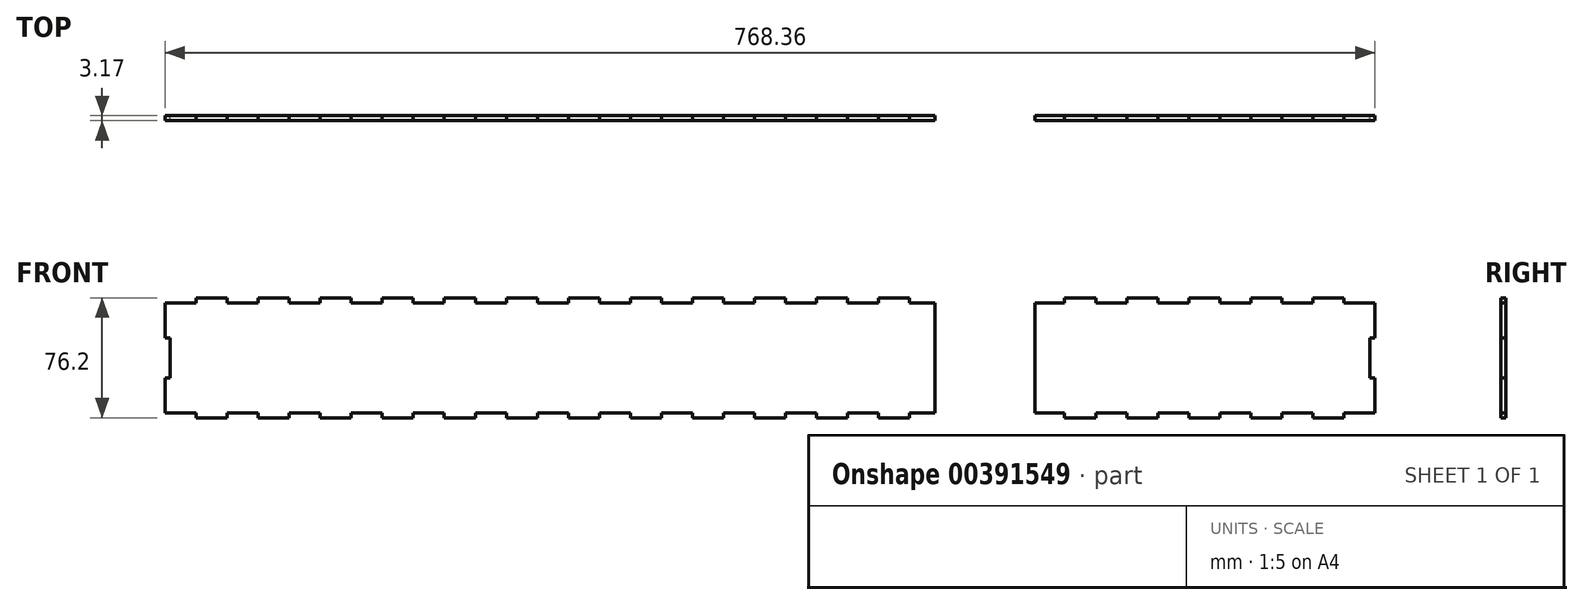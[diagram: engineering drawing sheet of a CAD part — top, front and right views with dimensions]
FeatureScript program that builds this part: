
annotation { "Feature Type Name" : "Feature", "Feature Type Description" : "" }
export const myFeature = defineFeature(function(context is Context, id is Id, definition is map)
    precondition{}
    {
        {
            var Q0;
            Q0=qCreatedBy(makeId("Front.planeOp"),FACE);
            var sketch = newSketch(context, id + "F0", { "sketchPlane" : qUnion([Q0])});
            skPoint(sketch, "E0.middle", {"position": v(0, 0) * mm});
            skLineSegment(sketch, "E1", {"start": v(-384.18, 12.7) * mm, "end": v(-381, 12.7) * mm});
            skLineSegment(sketch, "E2", {"start": v(-381, 12.7) * mm, "end": v(-381, -12.7) * mm});
            skLineSegment(sketch, "E3", {"start": v(-381, -12.7) * mm, "end": v(-384.18, -12.7) * mm});
            skLineSegment(sketch, "E4", {"start": v(-384.18, 34.92) * mm, "end": v(-364.47, 34.92) * mm});
            skLineSegment(sketch, "E5", {"start": v(-364.47, 34.92) * mm, "end": v(-364.47, 38.1) * mm});
            skLineSegment(sketch, "E6", {"start": v(-364.47, 38.1) * mm, "end": v(-344.77, 38.1) * mm});
            skLineSegment(sketch, "E7", {"start": v(-344.77, 38.1) * mm, "end": v(-344.77, 34.93) * mm});
            skLineSegment(sketch, "E8", {"start": v(-384.18, 38.1) * mm, "end": v(384.17, 38.1) * mm, "construction": true});
            skLineSegment(sketch, "E9.1.0.0", {"start": v(-344.77, 34.92) * mm, "end": v(-325.07, 34.92) * mm});
            skLineSegment(sketch, "E9.1.0.1", {"start": v(-325.07, 34.92) * mm, "end": v(-325.07, 38.1) * mm});
            skLineSegment(sketch, "E9.1.0.2", {"start": v(-325.07, 38.1) * mm, "end": v(-305.37, 38.1) * mm});
            skLineSegment(sketch, "E9.1.0.3", {"start": v(-305.37, 38.1) * mm, "end": v(-305.37, 34.93) * mm});
            skLineSegment(sketch, "E9.2.0.0", {"start": v(-305.37, 34.92) * mm, "end": v(-285.67, 34.92) * mm});
            skLineSegment(sketch, "E9.2.0.1", {"start": v(-285.67, 34.92) * mm, "end": v(-285.67, 38.1) * mm});
            skLineSegment(sketch, "E9.2.0.2", {"start": v(-285.67, 38.1) * mm, "end": v(-265.97, 38.1) * mm});
            skLineSegment(sketch, "E9.2.0.3", {"start": v(-265.97, 38.1) * mm, "end": v(-265.97, 34.93) * mm});
            skLineSegment(sketch, "E9.3.0.0", {"start": v(-265.97, 34.92) * mm, "end": v(-246.27, 34.92) * mm});
            skLineSegment(sketch, "E9.3.0.1", {"start": v(-246.27, 34.92) * mm, "end": v(-246.27, 38.1) * mm});
            skLineSegment(sketch, "E9.3.0.2", {"start": v(-246.27, 38.1) * mm, "end": v(-226.56, 38.1) * mm});
            skLineSegment(sketch, "E9.3.0.3", {"start": v(-226.56, 38.1) * mm, "end": v(-226.56, 34.93) * mm});
            skLineSegment(sketch, "E9.4.0.0", {"start": v(-226.56, 34.92) * mm, "end": v(-206.86, 34.92) * mm});
            skLineSegment(sketch, "E9.4.0.1", {"start": v(-206.86, 34.92) * mm, "end": v(-206.86, 38.1) * mm});
            skLineSegment(sketch, "E9.4.0.2", {"start": v(-206.86, 38.1) * mm, "end": v(-187.16, 38.1) * mm});
            skLineSegment(sketch, "E9.4.0.3", {"start": v(-187.16, 38.1) * mm, "end": v(-187.16, 34.93) * mm});
            skLineSegment(sketch, "E9.5.0.0", {"start": v(-187.16, 34.92) * mm, "end": v(-167.46, 34.92) * mm});
            skLineSegment(sketch, "E9.5.0.1", {"start": v(-167.46, 34.92) * mm, "end": v(-167.46, 38.1) * mm});
            skLineSegment(sketch, "E9.5.0.2", {"start": v(-167.46, 38.1) * mm, "end": v(-147.76, 38.1) * mm});
            skLineSegment(sketch, "E9.5.0.3", {"start": v(-147.76, 38.1) * mm, "end": v(-147.76, 34.93) * mm});
            skLineSegment(sketch, "E9.6.0.0", {"start": v(-147.76, 34.92) * mm, "end": v(-128.06, 34.92) * mm});
            skLineSegment(sketch, "E9.6.0.1", {"start": v(-128.06, 34.92) * mm, "end": v(-128.06, 38.1) * mm});
            skLineSegment(sketch, "E9.6.0.2", {"start": v(-128.06, 38.1) * mm, "end": v(-108.36, 38.1) * mm});
            skLineSegment(sketch, "E9.6.0.3", {"start": v(-108.36, 38.1) * mm, "end": v(-108.36, 34.93) * mm});
            skLineSegment(sketch, "E9.7.0.0", {"start": v(-108.36, 34.92) * mm, "end": v(-88.66, 34.92) * mm});
            skLineSegment(sketch, "E9.7.0.1", {"start": v(-88.66, 34.92) * mm, "end": v(-88.66, 38.1) * mm});
            skLineSegment(sketch, "E9.7.0.2", {"start": v(-88.66, 38.1) * mm, "end": v(-68.95, 38.1) * mm});
            skLineSegment(sketch, "E9.7.0.3", {"start": v(-68.95, 38.1) * mm, "end": v(-68.95, 34.93) * mm});
            skLineSegment(sketch, "E9.8.0.0", {"start": v(-68.95, 34.92) * mm, "end": v(-49.25, 34.92) * mm});
            skLineSegment(sketch, "E9.8.0.1", {"start": v(-49.25, 34.92) * mm, "end": v(-49.25, 38.1) * mm});
            skLineSegment(sketch, "E9.8.0.2", {"start": v(-49.25, 38.1) * mm, "end": v(-29.55, 38.1) * mm});
            skLineSegment(sketch, "E9.8.0.3", {"start": v(-29.55, 38.1) * mm, "end": v(-29.55, 34.93) * mm});
            skLineSegment(sketch, "E9.9.0.0", {"start": v(-29.55, 34.92) * mm, "end": v(-9.85, 34.92) * mm});
            skLineSegment(sketch, "E9.9.0.1", {"start": v(-9.85, 34.92) * mm, "end": v(-9.85, 38.1) * mm});
            skLineSegment(sketch, "E9.9.0.2", {"start": v(-9.85, 38.1) * mm, "end": v(9.85, 38.1) * mm});
            skLineSegment(sketch, "E9.9.0.3", {"start": v(9.85, 38.1) * mm, "end": v(9.85, 34.93) * mm});
            skLineSegment(sketch, "E9.10.0.0", {"start": v(9.85, 34.92) * mm, "end": v(29.55, 34.92) * mm});
            skLineSegment(sketch, "E9.10.0.1", {"start": v(29.55, 34.92) * mm, "end": v(29.55, 38.1) * mm});
            skLineSegment(sketch, "E9.10.0.2", {"start": v(29.55, 38.1) * mm, "end": v(49.25, 38.1) * mm});
            skLineSegment(sketch, "E9.10.0.3", {"start": v(49.25, 38.1) * mm, "end": v(49.25, 34.93) * mm});
            skLineSegment(sketch, "E9.11.0.0", {"start": v(49.25, 34.92) * mm, "end": v(68.95, 34.92) * mm});
            skLineSegment(sketch, "E9.11.0.1", {"start": v(68.95, 34.92) * mm, "end": v(68.95, 38.1) * mm});
            skLineSegment(sketch, "E9.11.0.2", {"start": v(68.95, 38.1) * mm, "end": v(88.66, 38.1) * mm});
            skLineSegment(sketch, "E9.11.0.3", {"start": v(88.66, 38.1) * mm, "end": v(88.66, 34.93) * mm});
            skLineSegment(sketch, "E9.12.0.0", {"start": v(88.66, 34.92) * mm, "end": v(108.36, 34.92) * mm});
            skLineSegment(sketch, "E9.12.0.1", {"start": v(108.36, 34.92) * mm, "end": v(108.36, 38.1) * mm});
            skLineSegment(sketch, "E9.12.0.2", {"start": v(108.36, 38.1) * mm, "end": v(128.06, 38.1) * mm});
            skLineSegment(sketch, "E9.12.0.3", {"start": v(128.06, 38.1) * mm, "end": v(128.06, 34.93) * mm});
            skLineSegment(sketch, "E9.13.0.0", {"start": v(128.06, 34.92) * mm, "end": v(147.76, 34.92) * mm});
            skLineSegment(sketch, "E9.13.0.1", {"start": v(147.76, 34.92) * mm, "end": v(147.76, 38.1) * mm});
            skLineSegment(sketch, "E9.13.0.2", {"start": v(147.76, 38.1) * mm, "end": v(167.46, 38.1) * mm});
            skLineSegment(sketch, "E9.13.0.3", {"start": v(167.46, 38.1) * mm, "end": v(167.46, 34.93) * mm});
            skLineSegment(sketch, "E9.14.0.0", {"start": v(167.46, 34.92) * mm, "end": v(187.16, 34.92) * mm});
            skLineSegment(sketch, "E9.14.0.1", {"start": v(187.16, 34.92) * mm, "end": v(187.16, 38.1) * mm});
            skLineSegment(sketch, "E9.14.0.2", {"start": v(187.16, 38.1) * mm, "end": v(206.86, 38.1) * mm});
            skLineSegment(sketch, "E9.14.0.3", {"start": v(206.86, 38.1) * mm, "end": v(206.86, 34.93) * mm});
            skLineSegment(sketch, "E9.15.0.0", {"start": v(206.86, 34.92) * mm, "end": v(226.56, 34.92) * mm});
            skLineSegment(sketch, "E9.15.0.1", {"start": v(226.56, 34.92) * mm, "end": v(226.56, 38.1) * mm});
            skLineSegment(sketch, "E9.15.0.2", {"start": v(226.56, 38.1) * mm, "end": v(246.27, 38.1) * mm});
            skLineSegment(sketch, "E9.15.0.3", {"start": v(246.27, 38.1) * mm, "end": v(246.27, 34.93) * mm});
            skLineSegment(sketch, "E9.16.0.0", {"start": v(246.27, 34.92) * mm, "end": v(265.97, 34.92) * mm});
            skLineSegment(sketch, "E9.16.0.1", {"start": v(265.97, 34.92) * mm, "end": v(265.97, 38.1) * mm});
            skLineSegment(sketch, "E9.16.0.2", {"start": v(265.97, 38.1) * mm, "end": v(285.67, 38.1) * mm});
            skLineSegment(sketch, "E9.16.0.3", {"start": v(285.67, 38.1) * mm, "end": v(285.67, 34.93) * mm});
            skLineSegment(sketch, "E9.17.0.0", {"start": v(285.67, 34.92) * mm, "end": v(305.37, 34.92) * mm});
            skLineSegment(sketch, "E9.17.0.1", {"start": v(305.37, 34.92) * mm, "end": v(305.37, 38.1) * mm});
            skLineSegment(sketch, "E9.17.0.2", {"start": v(305.37, 38.1) * mm, "end": v(325.07, 38.1) * mm});
            skLineSegment(sketch, "E9.17.0.3", {"start": v(325.07, 38.1) * mm, "end": v(325.07, 34.93) * mm});
            skLineSegment(sketch, "E9.18.0.0", {"start": v(325.07, 34.92) * mm, "end": v(344.77, 34.92) * mm});
            skLineSegment(sketch, "E9.18.0.1", {"start": v(344.77, 34.92) * mm, "end": v(344.77, 38.1) * mm});
            skLineSegment(sketch, "E9.18.0.2", {"start": v(344.77, 38.1) * mm, "end": v(364.47, 38.1) * mm});
            skLineSegment(sketch, "E9.18.0.3", {"start": v(364.47, 38.1) * mm, "end": v(364.47, 34.93) * mm});
            skLineSegment(sketch, "E9.19.0.0", {"start": v(364.47, 34.92) * mm, "end": v(384.18, 34.92) * mm});
            skLineSegment(sketch, "E9.direction1", {"start": v(-384.18, 34.92) * mm, "end": v(-344.77, 34.92) * mm, "construction": true});
            skLineSegment(sketch, "E10", {"start": v(-384.18, 34.92) * mm, "end": v(-384.18, 12.7) * mm});
            skLineSegment(sketch, "E11.MirrorCS", {"start": v(384.18, 12.7) * mm, "end": v(381, 12.7) * mm});
            skLineSegment(sketch, "E12.MirrorCS", {"start": v(381, -12.7) * mm, "end": v(384.18, -12.7) * mm});
            skLineSegment(sketch, "E13.MirrorCS", {"start": v(384.18, 34.92) * mm, "end": v(384.18, 12.7) * mm});
            skLineSegment(sketch, "E14.MirrorCS", {"start": v(381, 12.7) * mm, "end": v(381, -12.7) * mm});
            skLineSegment(sketch, "E15", {"start": v(130.17, 12.7) * mm, "end": v(130.17, -9.64) * mm, "construction": true});
            skLineSegment(sketch, "E16.MirrorCS", {"start": v(-285.67, -34.92) * mm, "end": v(-285.67, -38.1) * mm});
            skLineSegment(sketch, "E17.MirrorCS", {"start": v(-246.27, -34.92) * mm, "end": v(-246.27, -38.1) * mm});
            skLineSegment(sketch, "E18.MirrorCS", {"start": v(226.56, -34.92) * mm, "end": v(226.56, -38.1) * mm});
            skLineSegment(sketch, "E19.MirrorCS", {"start": v(68.95, -34.92) * mm, "end": v(68.95, -38.1) * mm});
            skLineSegment(sketch, "E20.MirrorCS", {"start": v(-88.66, -34.92) * mm, "end": v(-88.66, -38.1) * mm});
            skLineSegment(sketch, "E21.MirrorCS", {"start": v(-344.77, -38.1) * mm, "end": v(-344.77, -34.93) * mm});
            skLineSegment(sketch, "E22.MirrorCS", {"start": v(-325.07, -34.92) * mm, "end": v(-325.07, -38.1) * mm});
            skLineSegment(sketch, "E23.MirrorCS", {"start": v(-265.97, -38.1) * mm, "end": v(-265.97, -34.93) * mm});
            skLineSegment(sketch, "E24.MirrorCS", {"start": v(364.47, -38.1) * mm, "end": v(364.47, -34.93) * mm});
            skLineSegment(sketch, "E25.MirrorCS", {"start": v(206.86, -38.1) * mm, "end": v(206.86, -34.93) * mm});
            skLineSegment(sketch, "E26.MirrorCS", {"start": v(49.25, -38.1) * mm, "end": v(49.25, -34.93) * mm});
            skLineSegment(sketch, "E27.MirrorCS", {"start": v(-108.36, -38.1) * mm, "end": v(-108.36, -34.93) * mm});
            skLineSegment(sketch, "E28.MirrorCS", {"start": v(108.36, -34.92) * mm, "end": v(108.36, -38.1) * mm});
            skLineSegment(sketch, "E29.MirrorCS", {"start": v(-49.25, -34.92) * mm, "end": v(-49.25, -38.1) * mm});
            skLineSegment(sketch, "E30.MirrorCS", {"start": v(-206.86, -34.92) * mm, "end": v(-206.86, -38.1) * mm});
            skLineSegment(sketch, "E31.MirrorCS", {"start": v(265.97, -34.92) * mm, "end": v(265.97, -38.1) * mm});
            skLineSegment(sketch, "E32.MirrorCS", {"start": v(128.06, -38.1) * mm, "end": v(128.06, -34.93) * mm});
            skLineSegment(sketch, "E33.MirrorCS", {"start": v(-29.55, -38.1) * mm, "end": v(-29.55, -34.93) * mm});
            skLineSegment(sketch, "E34.MirrorCS", {"start": v(-187.16, -38.1) * mm, "end": v(-187.16, -34.93) * mm});
            skLineSegment(sketch, "E35.MirrorCS", {"start": v(285.67, -38.1) * mm, "end": v(285.67, -34.93) * mm});
            skLineSegment(sketch, "E36.MirrorCS", {"start": v(147.76, -34.92) * mm, "end": v(147.76, -38.1) * mm});
            skLineSegment(sketch, "E37.MirrorCS", {"start": v(-9.85, -34.92) * mm, "end": v(-9.85, -38.1) * mm});
            skLineSegment(sketch, "E38.MirrorCS", {"start": v(-167.46, -34.92) * mm, "end": v(-167.46, -38.1) * mm});
            skLineSegment(sketch, "E39.MirrorCS", {"start": v(305.37, -34.92) * mm, "end": v(305.37, -38.1) * mm});
            skLineSegment(sketch, "E40.MirrorCS", {"start": v(344.77, -34.92) * mm, "end": v(344.77, -38.1) * mm});
            skLineSegment(sketch, "E41.MirrorCS", {"start": v(187.16, -34.92) * mm, "end": v(187.16, -38.1) * mm});
            skLineSegment(sketch, "E42.MirrorCS", {"start": v(29.55, -34.92) * mm, "end": v(29.55, -38.1) * mm});
            skLineSegment(sketch, "E43.MirrorCS", {"start": v(-128.06, -34.92) * mm, "end": v(-128.06, -38.1) * mm});
            skLineSegment(sketch, "E44.MirrorCS", {"start": v(-364.47, -34.92) * mm, "end": v(-364.47, -38.1) * mm});
            skLineSegment(sketch, "E45.MirrorCS", {"start": v(-226.56, -38.1) * mm, "end": v(-226.56, -34.93) * mm});
            skLineSegment(sketch, "E46.MirrorCS", {"start": v(246.27, -38.1) * mm, "end": v(246.27, -34.93) * mm});
            skLineSegment(sketch, "E47.MirrorCS", {"start": v(88.66, -38.1) * mm, "end": v(88.66, -34.93) * mm});
            skLineSegment(sketch, "E48.MirrorCS", {"start": v(-68.95, -38.1) * mm, "end": v(-68.95, -34.93) * mm});
            skLineSegment(sketch, "E49.MirrorCS", {"start": v(325.07, -38.1) * mm, "end": v(325.07, -34.93) * mm});
            skLineSegment(sketch, "E50.MirrorCS", {"start": v(167.46, -38.1) * mm, "end": v(167.46, -34.93) * mm});
            skLineSegment(sketch, "E51.MirrorCS", {"start": v(9.85, -38.1) * mm, "end": v(9.85, -34.93) * mm});
            skLineSegment(sketch, "E52.MirrorCS", {"start": v(-147.76, -38.1) * mm, "end": v(-147.76, -34.93) * mm});
            skLineSegment(sketch, "E53.MirrorCS", {"start": v(-305.37, -38.1) * mm, "end": v(-305.37, -34.93) * mm});
            skLineSegment(sketch, "E54.MirrorCS", {"start": v(-384.18, -34.92) * mm, "end": v(-364.47, -34.92) * mm});
            skLineSegment(sketch, "E55.MirrorCS", {"start": v(-364.47, -38.1) * mm, "end": v(-344.77, -38.1) * mm});
            skLineSegment(sketch, "E56.MirrorCS", {"start": v(-325.07, -38.1) * mm, "end": v(-305.37, -38.1) * mm});
            skLineSegment(sketch, "E57.MirrorCS", {"start": v(-246.27, -38.1) * mm, "end": v(-226.56, -38.1) * mm});
            skLineSegment(sketch, "E58.MirrorCS", {"start": v(226.56, -38.1) * mm, "end": v(246.27, -38.1) * mm});
            skLineSegment(sketch, "E59.MirrorCS", {"start": v(68.95, -38.1) * mm, "end": v(88.66, -38.1) * mm});
            skLineSegment(sketch, "E60.MirrorCS", {"start": v(-88.66, -38.1) * mm, "end": v(-68.95, -38.1) * mm});
            skLineSegment(sketch, "E61.MirrorCS", {"start": v(-285.67, -38.1) * mm, "end": v(-265.97, -38.1) * mm});
            skLineSegment(sketch, "E62.MirrorCS", {"start": v(344.77, -38.1) * mm, "end": v(364.47, -38.1) * mm});
            skLineSegment(sketch, "E63.MirrorCS", {"start": v(187.16, -38.1) * mm, "end": v(206.86, -38.1) * mm});
            skLineSegment(sketch, "E64.MirrorCS", {"start": v(29.55, -38.1) * mm, "end": v(49.25, -38.1) * mm});
            skLineSegment(sketch, "E65.MirrorCS", {"start": v(-128.06, -38.1) * mm, "end": v(-108.36, -38.1) * mm});
            skLineSegment(sketch, "E66.MirrorCS", {"start": v(108.36, -38.1) * mm, "end": v(128.06, -38.1) * mm});
            skLineSegment(sketch, "E67.MirrorCS", {"start": v(-49.25, -38.1) * mm, "end": v(-29.55, -38.1) * mm});
            skLineSegment(sketch, "E68.MirrorCS", {"start": v(-206.86, -38.1) * mm, "end": v(-187.16, -38.1) * mm});
            skLineSegment(sketch, "E69.MirrorCS", {"start": v(265.97, -38.1) * mm, "end": v(285.67, -38.1) * mm});
            skLineSegment(sketch, "E70.MirrorCS", {"start": v(147.76, -38.1) * mm, "end": v(167.46, -38.1) * mm});
            skLineSegment(sketch, "E71.MirrorCS", {"start": v(-9.85, -38.1) * mm, "end": v(9.85, -38.1) * mm});
            skLineSegment(sketch, "E72.MirrorCS", {"start": v(-167.46, -38.1) * mm, "end": v(-147.76, -38.1) * mm});
            skLineSegment(sketch, "E73.MirrorCS", {"start": v(305.37, -38.1) * mm, "end": v(325.07, -38.1) * mm});
            skLineSegment(sketch, "E74.MirrorCS", {"start": v(-305.37, -34.92) * mm, "end": v(-285.67, -34.92) * mm});
            skLineSegment(sketch, "E75.MirrorCS", {"start": v(-384.18, -34.92) * mm, "end": v(-344.77, -34.92) * mm, "construction": true});
            skLineSegment(sketch, "E76.MirrorCS", {"start": v(-384.18, -38.1) * mm, "end": v(384.17, -38.1) * mm, "construction": true});
            skLineSegment(sketch, "E77.MirrorCS", {"start": v(-344.77, -34.92) * mm, "end": v(-325.07, -34.92) * mm});
            skLineSegment(sketch, "E78.MirrorCS", {"start": v(-265.97, -34.92) * mm, "end": v(-246.27, -34.92) * mm});
            skLineSegment(sketch, "E79.MirrorCS", {"start": v(364.47, -34.92) * mm, "end": v(384.18, -34.92) * mm});
            skLineSegment(sketch, "E80.MirrorCS", {"start": v(206.86, -34.92) * mm, "end": v(226.56, -34.92) * mm});
            skLineSegment(sketch, "E81.MirrorCS", {"start": v(49.25, -34.92) * mm, "end": v(68.95, -34.92) * mm});
            skLineSegment(sketch, "E82.MirrorCS", {"start": v(-108.36, -34.92) * mm, "end": v(-88.66, -34.92) * mm});
            skLineSegment(sketch, "E83.MirrorCS", {"start": v(-226.56, -34.92) * mm, "end": v(-206.86, -34.92) * mm});
            skLineSegment(sketch, "E84.MirrorCS", {"start": v(246.27, -34.92) * mm, "end": v(265.97, -34.92) * mm});
            skLineSegment(sketch, "E85.MirrorCS", {"start": v(88.66, -34.92) * mm, "end": v(108.36, -34.92) * mm});
            skLineSegment(sketch, "E86.MirrorCS", {"start": v(-68.95, -34.92) * mm, "end": v(-49.25, -34.92) * mm});
            skLineSegment(sketch, "E87.MirrorCS", {"start": v(128.06, -34.92) * mm, "end": v(147.76, -34.92) * mm});
            skLineSegment(sketch, "E88.MirrorCS", {"start": v(-29.55, -34.92) * mm, "end": v(-9.85, -34.92) * mm});
            skLineSegment(sketch, "E89.MirrorCS", {"start": v(-187.16, -34.92) * mm, "end": v(-167.46, -34.92) * mm});
            skLineSegment(sketch, "E90.MirrorCS", {"start": v(285.67, -34.92) * mm, "end": v(305.37, -34.92) * mm});
            skLineSegment(sketch, "E91.MirrorCS", {"start": v(325.07, -34.92) * mm, "end": v(344.77, -34.92) * mm});
            skLineSegment(sketch, "E92.MirrorCS", {"start": v(167.46, -34.92) * mm, "end": v(187.16, -34.92) * mm});
            skLineSegment(sketch, "E93.MirrorCS", {"start": v(9.85, -34.92) * mm, "end": v(29.55, -34.92) * mm});
            skLineSegment(sketch, "E94.MirrorCS", {"start": v(-147.76, -34.92) * mm, "end": v(-128.06, -34.92) * mm});
            skLineSegment(sketch, "E95", {"start": v(384.18, -34.92) * mm, "end": v(384.18, -12.7) * mm});
            skLineSegment(sketch, "E96", {"start": v(384.17, -38.1) * mm, "end": v(384.17, 38.1) * mm, "construction": true});
            skLineSegment(sketch, "E97", {"start": v(-384.18, -12.7) * mm, "end": v(-384.18, -34.92) * mm});
            skLineSegment(sketch, "E98", {"start": v(-384.18, 38.1) * mm, "end": v(-384.18, -38.1) * mm, "construction": true});
            skLineSegment(sketch, "E99", {"start": v(142.87, 13.12) * mm, "end": v(142.87, -9.98) * mm, "construction": true});
            skLineSegment(sketch, "E100", {"start": v(104.77, 12.91) * mm, "end": v(104.77, -8.97) * mm, "construction": true});
            skLineSegment(sketch, "E101", {"start": v(168.27, 14.13) * mm, "end": v(168.27, -7.75) * mm, "construction": true});
            skLineSegment(sketch, "E102", {"start": v(104.77, -8.97) * mm, "end": v(104.77, -62.23) * mm, "construction": true});
            skLineSegment(sketch, "E103", {"start": v(168.27, 14.13) * mm, "end": v(168.27, 69.37) * mm, "construction": true});
            skLineSegment(sketch, "E104.bottom", {"start": v(104.77, -62.23) * mm, "end": v(168.27, -62.23) * mm});
            skLineSegment(sketch, "E104.top", {"start": v(104.77, 69.37) * mm, "end": v(168.27, 69.37) * mm});
            skLineSegment(sketch, "E104.left", {"start": v(104.77, -62.23) * mm, "end": v(104.77, 69.37) * mm});
            skLineSegment(sketch, "E104.right", {"start": v(168.27, -62.23) * mm, "end": v(168.27, 69.37) * mm});
            skSolve(sketch);
        }
        {
            var Q0;
            Q0=makeQuery(id+"F0.imprint","IMPRINT",FACE,{"disambiguationData":[TD([[makeQuery(id+"F0.imprint","IMPRINT",EDGE,{"derivedFrom":sQuery(id+"F0.wireOp",EDGE,"E1")}),1.0]])]});
            var Q1;
            {var subQ4=sQuery(id+"F0.wireOp",EDGE,"E9.14.0.1");Q1=makeQuery(id+"F0.imprint","IMPRINT",FACE,{"disambiguationData":[TD([[makeQuery(id+"F0.imprint","IMPRINT",EDGE,{"derivedFrom":subQ4}),-1.0]])]});}
            extrude(context, id + "F1", {"entities" : qUnion([Q0, Q1]), "depth" : 3.17 * mm});
        }
    });
